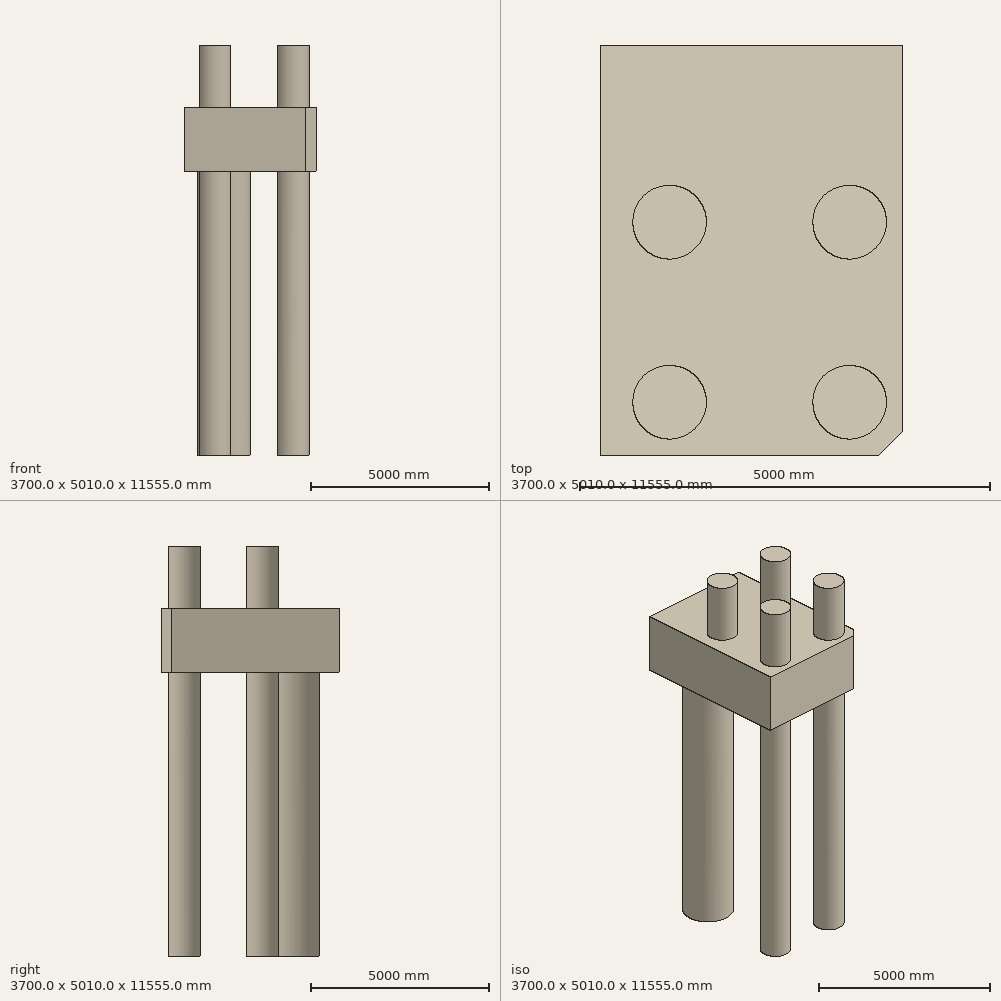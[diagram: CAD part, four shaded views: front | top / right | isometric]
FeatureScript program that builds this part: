
annotation { "Feature Type Name" : "Feature", "Feature Type Description" : "" }
export const myFeature = defineFeature(function(context is Context, id is Id, definition is map)
    precondition{}
    {
        {
            var Q0;
            Q0=qCreatedBy(makeId("Top.planeOp"),FACE);
            var sketch = newSketch(context, id + "F0", { "sketchPlane" : qUnion([Q0])});
            skLineSegment(sketch, "E0", {"start": v(-95.05, 6359.43) * mm, "end": v(-95.05, 1349.43) * mm});
            skLineSegment(sketch, "E1", {"start": v(-95.05, 6359.43) * mm, "end": v(3604.95, 6359.43) * mm});
            skLineSegment(sketch, "E2", {"start": v(3604.95, 6359.43) * mm, "end": v(3604.95, 1638.27) * mm});
            skLineSegment(sketch, "E3", {"start": v(-95.05, 1349.43) * mm, "end": v(3316.12, 1349.43) * mm});
            skLineSegment(sketch, "E4", {"start": v(3316.12, 1349.43) * mm, "end": v(3604.95, 1638.27) * mm});
            skSolve(sketch);
        }
        {
            var Q0;
            Q0=makeQuery(id+"F0.imprint","IMPRINT",FACE,{"disambiguationData":[TD([[makeQuery(id+"F0.imprint","IMPRINT",EDGE,{"derivedFrom":sQuery(id+"F0.wireOp",EDGE,"E0")}),1.0]])]});
            extrude(context, id + "F1", {"entities" : qUnion([Q0]), "endBound" : BoundingType.SYMMETRIC, "depth" : 1800 * mm, "offsetDistance" : 25 * mm});
        }
        {
            var Q0;
            Q0=makeQuery(id+"F1.opExtrude","CAP_FACE",FACE,{"disambiguationData":[OSD([sQuery(id+"F0.wireOp",EDGE,"E0"),sQuery(id+"F0.wireOp",EDGE,"E1"),sQuery(id+"F0.wireOp",EDGE,"E2"),sQuery(id+"F0.wireOp",EDGE,"E3"),sQuery(id+"F0.wireOp",EDGE,"E4")])],"isStart":false});
            var sketch = newSketch(context, id + "F2", { "sketchPlane" : qUnion([Q0])});
            skCircle(sketch, "E5", {"center": v(754.95, 4199.43) * mm, "radius": 450 * mm});
            skCircle(sketch, "E6", {"center": v(2954.95, 4199.43) * mm, "radius": 450 * mm});
            skCircle(sketch, "E7", {"center": v(2954.95, 1999.43) * mm, "radius": 450 * mm});
            skCircle(sketch, "E8", {"center": v(754.95, 1999.43) * mm, "radius": 450 * mm});
            skSolve(sketch);
        }
        {
            var Q0;
            Q0=makeQuery(id+"F2.imprint","IMPRINT",FACE,{"disambiguationData":[TD([[makeQuery(id+"F2.imprint","IMPRINT",EDGE,{"derivedFrom":sQuery(id+"F2.wireOp",EDGE,"E5")}),1.0]])]});
            var Q1;
            Q1=makeQuery(id+"F2.imprint","IMPRINT",FACE,{"disambiguationData":[TD([[makeQuery(id+"F2.imprint","IMPRINT",EDGE,{"derivedFrom":sQuery(id+"F2.wireOp",EDGE,"E8")}),1.0]])]});
            var Q2;
            Q2=makeQuery(id+"F2.imprint","IMPRINT",FACE,{"disambiguationData":[TD([[makeQuery(id+"F2.imprint","IMPRINT",EDGE,{"derivedFrom":sQuery(id+"F2.wireOp",EDGE,"E6")}),1.0]])]});
            var Q3;
            Q3=makeQuery(id+"F2.imprint","IMPRINT",FACE,{"disambiguationData":[TD([[makeQuery(id+"F2.imprint","IMPRINT",EDGE,{"derivedFrom":sQuery(id+"F2.wireOp",EDGE,"E7")}),1.0]])]});
            extrude(context, id + "F3", {"entities" : qUnion([Q0, Q1, Q2, Q3]), "operationType" : NewBodyOperationType.ADD, "depth" : 1755 * mm, "offsetDistance" : 25 * mm});
        }
        {
            var Q0;
            Q0=makeQuery(id+"F1.opExtrude","CAP_FACE",FACE,{"disambiguationData":[OSD([sQuery(id+"F0.wireOp",EDGE,"E0"),sQuery(id+"F0.wireOp",EDGE,"E1"),sQuery(id+"F0.wireOp",EDGE,"E2"),sQuery(id+"F0.wireOp",EDGE,"E3"),sQuery(id+"F0.wireOp",EDGE,"E4")])],"isStart":true});
            var sketch = newSketch(context, id + "F4", { "sketchPlane" : qUnion([Q0])});
            skCircle(sketch, "E9", {"center": v(754.95, -1999.43) * mm, "radius": 450 * mm});
            skCircle(sketch, "E10", {"center": v(2954.95, -1999.43) * mm, "radius": 450 * mm});
            skCircle(sketch, "E11", {"center": v(2954.95, -4199.43) * mm, "radius": 450 * mm});
            skCircle(sketch, "E12", {"center": v(1004.95, -5045.43) * mm, "radius": 750 * mm});
            skSolve(sketch);
        }
        {
            var Q0;
            Q0=makeQuery(id+"F4.imprint","IMPRINT",FACE,{"disambiguationData":[TD([[makeQuery(id+"F4.imprint","IMPRINT",EDGE,{"derivedFrom":sQuery(id+"F4.wireOp",EDGE,"E9")}),1.0]])]});
            var Q1;
            Q1=makeQuery(id+"F4.imprint","IMPRINT",FACE,{"disambiguationData":[TD([[makeQuery(id+"F4.imprint","IMPRINT",EDGE,{"derivedFrom":sQuery(id+"F4.wireOp",EDGE,"E10")}),1.0]])]});
            var Q2;
            Q2=makeQuery(id+"F4.imprint","IMPRINT",FACE,{"disambiguationData":[TD([[makeQuery(id+"F4.imprint","IMPRINT",EDGE,{"derivedFrom":sQuery(id+"F4.wireOp",EDGE,"E11")}),1.0]])]});
            var Q3;
            Q3=makeQuery(id+"F4.imprint","IMPRINT",FACE,{"disambiguationData":[TD([[makeQuery(id+"F4.imprint","IMPRINT",EDGE,{"derivedFrom":sQuery(id+"F4.wireOp",EDGE,"E12")}),1.0]])]});
            extrude(context, id + "F5", {"entities" : qUnion([Q0, Q1, Q2, Q3]), "operationType" : NewBodyOperationType.ADD, "depth" : 8000 * mm, "offsetDistance" : 25 * mm});
        }
        {
            var Q0;
            Q0=sQuery(id+"F4.wireOp",EDGE,"E12");
            extrude(context, id + "F6", {"bodyType" : ToolBodyType.SURFACE, "surfaceEntities" : qUnion([Q0]), "oppositeDirection" : true, "depth" : 7100 * mm, "offsetDistance" : 25 * mm});
        }
    });
